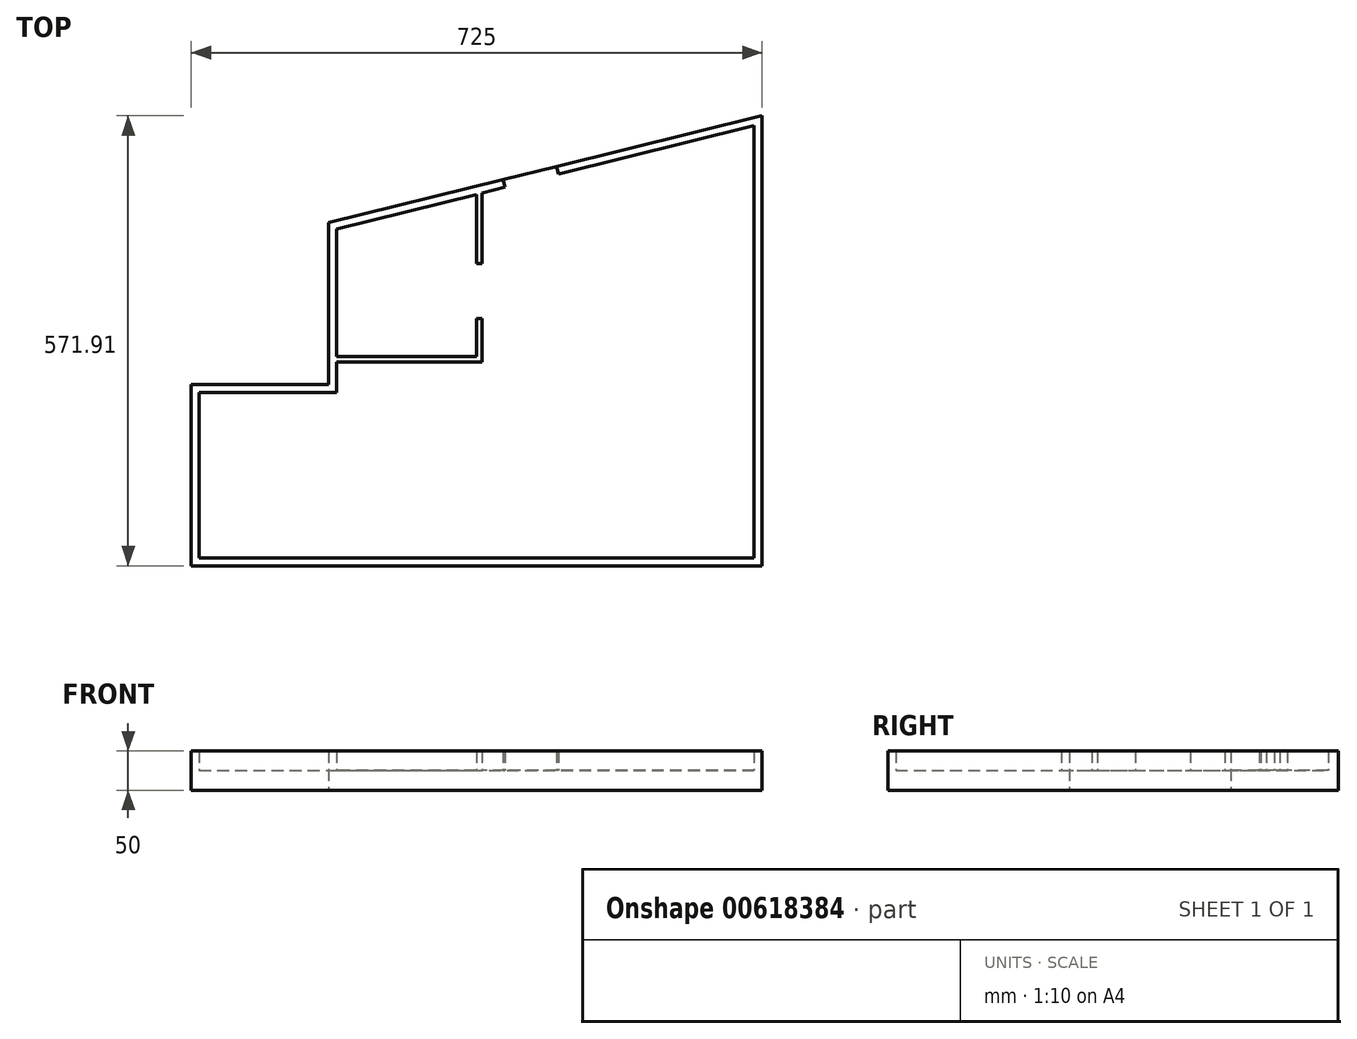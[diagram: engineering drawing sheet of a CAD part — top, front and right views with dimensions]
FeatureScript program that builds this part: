
annotation { "Feature Type Name" : "Feature", "Feature Type Description" : "" }
export const myFeature = defineFeature(function(context is Context, id is Id, definition is map)
    precondition{}
    {
        {
            var Q0;
            Q0=qCreatedBy(makeId("Top.planeOp"),FACE);
            var sketch = newSketch(context, id + "F0", { "sketchPlane" : qUnion([Q0])});
            skLineSegment(sketch, "E0", {"start": v(0, 0) * mm, "end": v(705, 0) * mm});
            skLineSegment(sketch, "E1", {"start": v(0, 0) * mm, "end": v(0, 210.3) * mm});
            skLineSegment(sketch, "E2", {"start": v(0, 210.3) * mm, "end": v(174.5, 210.3) * mm});
            skLineSegment(sketch, "E3", {"start": v(174.5, 210.3) * mm, "end": v(174.5, 256.27) * mm});
            skLineSegment(sketch, "E4", {"start": v(174.5, 256.27) * mm, "end": v(352.5, 256.27) * mm});
            skPoint(sketch, "E5", {"position": v(352.5, 0) * mm});
            skLineSegment(sketch, "E6", {"start": v(352.5, 256.27) * mm, "end": v(352.5, 462) * mm});
            skLineSegment(sketch, "E7", {"start": v(174.5, 256.27) * mm, "end": v(174.5, 418) * mm});
            skLineSegment(sketch, "E8", {"start": v(705, 0) * mm, "end": v(705, 549.13) * mm});
            skLineSegment(sketch, "E9", {"start": v(705, 549.13) * mm, "end": v(174.5, 418) * mm});
            skLineSegment(sketch, "E10.0", {"start": v(359.5, 249.27) * mm, "end": v(359.5, 451.62) * mm});
            skLineSegment(sketch, "E10.1", {"start": v(174.5, 249.27) * mm, "end": v(359.5, 249.27) * mm});
            skPoint(sketch, "E11", {"position": v(352.5, 304.08) * mm});
            skPoint(sketch, "E12", {"position": v(359.5, 304.08) * mm});
            skPoint(sketch, "E13", {"position": v(352.5, 374.08) * mm});
            skPoint(sketch, "E14", {"position": v(359.5, 374.08) * mm});
            skLineSegment(sketch, "E15", {"start": v(352.5, 304.08) * mm, "end": v(359.5, 304.08) * mm});
            skLineSegment(sketch, "E16", {"start": v(352.5, 374.08) * mm, "end": v(359.5, 374.08) * mm});
            skLineSegment(sketch, "E17.0", {"start": v(-10, -10) * mm, "end": v(715, -10) * mm});
            skLineSegment(sketch, "E17.1", {"start": v(715, -10) * mm, "end": v(715, 561.9) * mm});
            skLineSegment(sketch, "E17.2", {"start": v(-10, 220.3) * mm, "end": v(164.5, 220.3) * mm});
            skLineSegment(sketch, "E17.3", {"start": v(164.5, 220.3) * mm, "end": v(164.5, 256.27) * mm});
            skLineSegment(sketch, "E17.4", {"start": v(164.5, 256.27) * mm, "end": v(164.5, 425.83) * mm});
            skLineSegment(sketch, "E17.5", {"start": v(-10, -10) * mm, "end": v(-10, 220.3) * mm});
            skLineSegment(sketch, "E17.6", {"start": v(715, 561.9) * mm, "end": v(164.5, 425.83) * mm});
            skPoint(sketch, "E18", {"position": v(386.26, 480.65) * mm});
            skPoint(sketch, "E19", {"position": v(388.66, 470.94) * mm});
            skPoint(sketch, "E20", {"position": v(454.22, 497.44) * mm});
            skLineSegment(sketch, "E21", {"start": v(386.26, 480.65) * mm, "end": v(388.66, 470.94) * mm});
            skPoint(sketch, "E22", {"position": v(456.62, 487.74) * mm});
            skLineSegment(sketch, "E23", {"start": v(456.62, 487.74) * mm, "end": v(454.22, 497.44) * mm});
            skLineSegment(sketch, "E24", {"start": v(359.5, 451.62) * mm, "end": v(359.5, 463.73) * mm});
            skSolve(sketch);
        }
        {
            var Q0;
            Q0=makeQuery(id+"F0.imprint","IMPRINT",FACE,{"disambiguationData":[TD([[makeQuery(id+"F0.imprint","IMPRINT",EDGE,{"derivedFrom":sQuery(id+"F0.wireOp",EDGE,"E0")}),1.0]])]});
            var Q1;
            {var subQ5=sQuery(id+"F0.wireOp",EDGE,"E4");Q1=makeQuery(id+"F0.imprint","IMPRINT",FACE,{"disambiguationData":[TD([[makeQuery(id+"F0.imprint","IMPRINT",EDGE,{"derivedFrom":subQ5}),1.0]])]});}
            var Q2;
            {var subQ0=sQuery(id+"F0.wireOp",EDGE,"E21");Q2=makeQuery(id+"F0.imprint","IMPRINT",FACE,{"disambiguationData":[TD([[makeQuery(id+"F0.imprint","IMPRINT",EDGE,{"derivedFrom":subQ0}),1.0]])]});}
            var Q3;
            {var subQ0=sQuery(id+"F0.wireOp",EDGE,"E15");Q3=makeQuery(id+"F0.imprint","IMPRINT",FACE,{"disambiguationData":[TD([[makeQuery(id+"F0.imprint","IMPRINT",EDGE,{"derivedFrom":subQ0}),1.0]])]});}
            extrude(context, id + "F1", {"entities" : qUnion([Q0, Q1, Q2, Q3]), "depth" : 25 * mm, "offsetDistance" : 25 * mm});
        }
        {
            var Q0;
            {var subQ0=sQuery(id+"F0.wireOp",EDGE,"E16");Q0=makeQuery(id+"F0.imprint","IMPRINT",FACE,{"disambiguationData":[TD([[makeQuery(id+"F0.imprint","IMPRINT",EDGE,{"derivedFrom":subQ0}),1.0]])]});}
            var Q1;
            {var subQ3=sQuery(id+"F0.wireOp",EDGE,"E4");Q1=makeQuery(id+"F0.imprint","IMPRINT",FACE,{"disambiguationData":[TD([[makeQuery(id+"F0.imprint","IMPRINT",EDGE,{"derivedFrom":subQ3}),-1.0]])]});}
            var Q2;
            Q2=makeQuery(id+"F0.imprint","IMPRINT",FACE,{"disambiguationData":[TD([[makeQuery(id+"F0.imprint","IMPRINT",EDGE,{"derivedFrom":sQuery(id+"F0.wireOp",EDGE,"E0")}),-1.0]])]});
            extrude(context, id + "F2", {"entities" : qUnion([Q0, Q1, Q2]), "operationType" : NewBodyOperationType.ADD, "depth" : 50 * mm, "offsetDistance" : 25 * mm});
        }
    });
